# Revit family: Lockers_Series-51-with-Bottom-Base_Lincora
name_source: partatom
category: Casework
units: mm (PartAtom-declared; Revit-internal decimal feet)

## family parameters
Always vertical = Yes
Cut with Voids When Loaded = No
Room Calculation Point = No
Shared = No
Work Plane-Based = No

## types (12) — shared parameters
CAD Details = https://www.arcat.com
Default Elevation = 0"
Hook Material = Aluminum
Keynote = 10 51 00
Manufacturer = Lincora
Max Depth = 28"
Max Height = 90"
Max Width = 48"
Min Depth = 12"
Min Height = 30 1/2"
Min Width = 9"
Model = Series 51
Product Page URL = https://www.arcat.com
Specification = https://www.arcat.com
URL = https://www.lincora.com

## per-type parameters (varying)
| type | Base Material | Body Material | Depth | Height | Hook Width | Incremet | Requested Depth | Requested Height | Requested Width | Width |
| Series 51_White | White | White | 28" | 90" | 46" | 8-Jan | 28" | 90" | 48" | 48" |
| Series 51_Nevada Beige | Nevada Beige | Nevada Beige | 12" | 30 1/2" | 7" |  | 0" | 0" | 0" | 9" |
| Series 51_Pearl Gray | Pearl Gray | Pearl Gray | 12" | 30 1/2" | 7" |  | 0" | 0" | 0" | 9" |
| Series 51_Aluminum Gray | Aluminum Gray | Aluminum Gray | 12" | 30 1/2" | 7" |  | 0" | 0" | 0" | 9" |
| Series 51_Platinum Gray | Platinum Gray | Platinum Gray | 12" | 30 1/2" | 7" |  | 0" | 0" | 0" | 9" |
| Series 51_Medium Gray | Medium Gray | Medium Gray | 12" | 30 1/2" | 7" |  | 0" | 0" | 0" | 9" |
| Series 51_Dark Gray | Dark Gray | Dark Gray | 12" | 30 1/2" | 7" |  | 0" | 0" | 0" | 9" |
| Series 51_Ocean Blue | Ocean Blue | Ocean Blue | 12" | 30 1/2" | 7" |  | 0" | 0" | 0" | 9" |
| Series 51_Azure Blue | Azure Blue | Azure Blue | 12" | 30 1/2" | 7" |  | 0" | 0" | 0" | 9" |
| Series 51_Dark Blue | Dark Blue | Dark Blue | 12" | 30 1/2" | 7" |  | 0" | 0" | 0" | 9" |
| Series 51_Black | Black | Black | 12" | 30 1/2" | 7" |  | 0" | 0" | 0" | 9" |
| Series 51_Red | Red | Red | 12" | 30 1/2" | 7" |  | 0" | 0" | 0" | 9" |

## geometry (parser evidence)
native form markers: Sweep x8
no freeform markers — native parametric forms only
